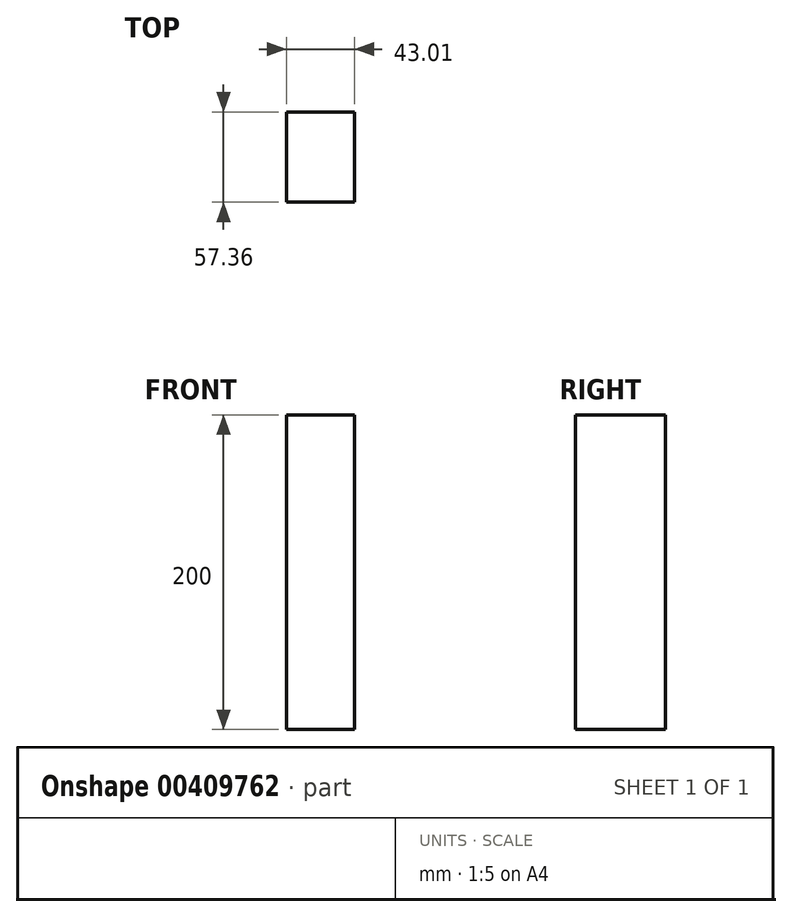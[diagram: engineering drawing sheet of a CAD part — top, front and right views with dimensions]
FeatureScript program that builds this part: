
annotation { "Feature Type Name" : "Feature", "Feature Type Description" : "" }
export const myFeature = defineFeature(function(context is Context, id is Id, definition is map)
    precondition{}
    {
        {
            var Q0;
            Q0=qCreatedBy(makeId("Top.planeOp"),FACE);
            var sketch = newSketch(context, id + "F0", { "sketchPlane" : qUnion([Q0])});
            skLineSegment(sketch, "E0.bottom", {"start": v(0, 0) * mm, "end": v(43, 0) * mm});
            skLineSegment(sketch, "E0.top", {"start": v(0, -57.36) * mm, "end": v(43, -57.36) * mm});
            skLineSegment(sketch, "E0.left", {"start": v(0, 0) * mm, "end": v(0, -57.36) * mm});
            skLineSegment(sketch, "E0.right", {"start": v(43, 0) * mm, "end": v(43, -57.36) * mm});
            skSolve(sketch);
        }
        {
            var Q0;
            Q0=makeQuery(id+"F0.imprint","IMPRINT",FACE,{"disambiguationData":[TD([[makeQuery(id+"F0.imprint","IMPRINT",EDGE,{"derivedFrom":sQuery(id+"F0.wireOp",EDGE,"E0.bottom")}),-1.0]])]});
            extrude(context, id + "F1", {"entities" : qUnion([Q0]), "depth" : 200 * mm});
        }
    });
